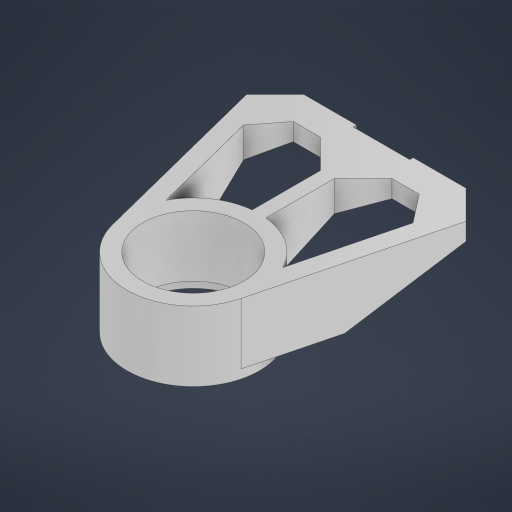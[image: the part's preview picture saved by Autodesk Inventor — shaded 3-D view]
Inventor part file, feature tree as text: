
AUTODESK INVENTOR PART (.ipt)
format: ipt  version: 2024 (Build 280153000, 153)  size: 297,984 bytes
history: native  units: mm
features: extrude x5, sketch x5, projected_geometry x5, chamfer x1
ambient origin geometry x8: Origin, YZ Plane, XZ Plane, XY Plane, X Axis, Y Axis, Z Axis, Center Point
bodies: Solid1 (feature_tree)
feature tree (16):
  extrude  "Extrusion1"  Depth=10.0mm TaperAngle=0.0deg
  extrude  "Extrusion2"  Depth=50.0mm
  extrude  "Extrusion3"  Depth=70.0mm TaperAngle=0.0deg
  extrude  "Extrusion5"  Depth=20.0mm
  chamfer  "Chamfer1"  Distance=20.0mm
  extrude  "Extrusion6"  Depth=33.0mm
  sketch  "Sketch1"  dims[d0=124.1mm d1=10.0mm d2=0.0mm]
  sketch  "Sketch2"  dims[d3=220.0mm d4=50.0mm]
  projected_geometry  "Projected Loop1"
  sketch  "Sketch3"  dims[d5=50.0mm d6=70.0mm d7=0.0mm]
  sketch  "Sketch4"  dims[d8=300.0mm d9=0.0mm d10=20.0mm]
  projected_geometry  "Projected Loop2"
  projected_geometry  "Projected Loop3"
  projected_geometry  "Projected Loop4"
  projected_geometry  "Projected Loop5"
  sketch  "Sketch7"  dims[d11=20.0mm d12=20.0mm d15=33.0mm d16=76.0mm d17=76.0mm d18=126.0mm d19=300.0mm d20=0.0mm d21=33.0mm d22=2.0mm d23=45.0deg d24=65.0mm d25=60.5mm d26=60.5mm d27=4.0mm d28=0.0mm]
